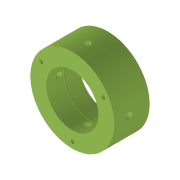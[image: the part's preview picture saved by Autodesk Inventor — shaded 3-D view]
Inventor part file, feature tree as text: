
AUTODESK INVENTOR PART (.ipt)
format: ipt  version: 2022 (Build 260153000, 153)  size: 239,616 bytes
history: native  units: mm
features: reference x14, other x8, sketch x7, extrude x5, projected_geometry x3, plane x2, revolve x1, hole x1, pattern_circular x1
ambient origin geometry x8: Origin, YZ Plane, XZ Plane, XY Plane, X Axis, Y Axis, Z Axis, Center Point
bodies: Volumenkörper1 (feature_tree)
feature tree (42):
  revolve  "Umdrehung1"
  sketch  "Skizze2"  dims[d5=0.5mm d6=10.0mm d7=0.0mm]
  plane  "Arbeitsebene1"
  extrude  "Extrusion1"  TaperAngle=360.0deg  [1 undecoded]
  hole  "Bohrung1"  [1 undecoded]
  extrude  "Extrusion2"  Depth=27.0mm
  extrude  "Extrusion3"  Depth=10.0mm
  sketch  "Skizze6"  dims[d22=0.2mm d24=24.0mm]
  plane  "Arbeitsebene2"
  extrude  "Extrusion4"  Depth=24.0mm
  extrude  "Extrusion5"  Depth=10.0mm
  pattern_circular  "Runde Anordnung1"  [2 undecoded]
  sketch  "Skizze1"  dims[d3=5.0mm d4=360.0deg]
  reference  "Referenz1"
  reference  "Referenz2"
  reference  "Referenz3"
  sketch  "Skizze3"  dims[d8=16.5mm]
  reference  "Referenz4"
  reference  "Referenz5"
  sketch  "Skizze4"  dims[d9=2.8mm d10=6.0mm d11=4.0mm d12=2.0mm d13=90.0deg d14=16.0mm d15=20.594885mm d18=27.0mm]
  reference  "Referenz6"
  reference  "Referenz7"
  reference  "Referenz8"
  sketch  "Skizze5"  dims[d19=10.0mm d20=0.0mm d21=0.1mm]
  reference  "Referenz9"
  reference  "Referenz10"
  reference  "Referenz11"
  projected_geometry  "Projizierte Kontur1"
  sketch  "Skizze7"  dims[d25=0.5mm d26=0.0mm d27=1.8mm d28=10.0mm d29=0.0mm d30=2.8mm d31=3.249767mm d32=1.624884mm d33=0.0mm d34=0.0mm d35=20.0mm d36=90.0deg]
  projected_geometry  "Projizierte Kontur2"
  projected_geometry  "Projizierte Kontur3"
  reference  "Referenz12"
  reference  "Referenz13"
  reference  "Referenz14"
  other  "Assembly_ETL_v0.iam"
  other  "50_ETL_Membrane_v0:1"
  other  "50_ETL_28by_coil:1"
  other  "50_ETL_Base_layer1_v0:1"
  other  "50_ETL_Spring_v0:3"
  other  "50_ETL_28by_coil:3"
  other  "50_Assembly_ETL_Mould:2"
  other  "50_ETL_Membrane_Mould_Upper_v0:1"
note: 4 required parameter values undecoded (feature->parameter linkage not recoverable at this tier; creation-order binding heuristic only, values carry confidence <= 0.55)
